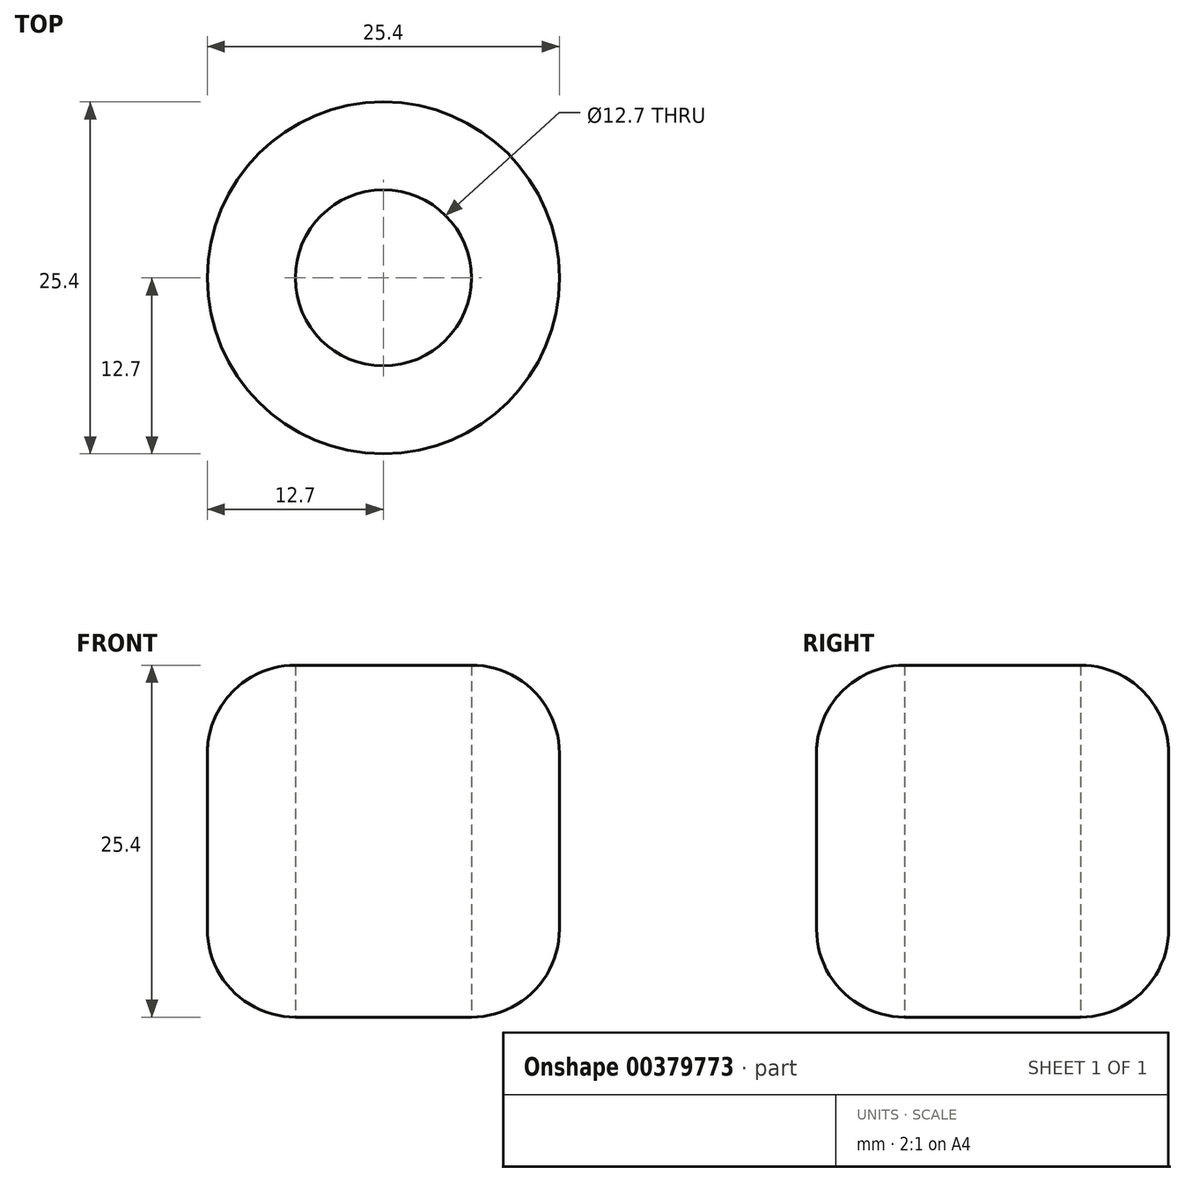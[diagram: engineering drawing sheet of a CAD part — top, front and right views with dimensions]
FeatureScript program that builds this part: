
annotation { "Feature Type Name" : "Feature", "Feature Type Description" : "" }
export const myFeature = defineFeature(function(context is Context, id is Id, definition is map)
    precondition{}
    {
        {
            var Q0;
            Q0=qCreatedBy(makeId("Top.planeOp"),FACE);
            var sketch = newSketch(context, id + "F0", { "sketchPlane" : qUnion([Q0])});
            skCircle(sketch, "E0", {"center": v(0, 0) * mm, "radius": 12.7 * mm});
            skSolve(sketch);
        }
        {
            var Q0;
            Q0 = qSketchRegion(id + "F0", true);
            extrude(context, id + "F1", {"entities" : qUnion([Q0]), "depth" : 25.4 * mm});
        }
        {
            var Q0;
            Q0=makeQuery(id+"F1.opExtrude","SWEPT_FACE",FACE,{"disambiguationData":[OSD([sQuery(id+"F0.wireOp",EDGE,"E0")])]});
            fillet(context, id + "F2", {"entities" : qUnion([Q0]), "radius" : 6.35 * mm, "tangentPropagation" : true, "allowEdgeOverflow" : false});
        }
        {
            var Q0;
            Q0=qCreatedBy(makeId("Top.planeOp"),FACE);
            var sketch = newSketch(context, id + "F3", { "sketchPlane" : qUnion([Q0])});
            skCircle(sketch, "E1", {"center": v(0, 0) * mm, "radius": 6.35 * mm});
            skSolve(sketch);
        }
        {
            var Q0;
            Q0 = qSketchRegion(id + "F3", true);
            extrude(context, id + "F4", {"entities" : qUnion([Q0]), "operationType" : NewBodyOperationType.REMOVE, "depth" : 25.4 * mm});
        }
    });
